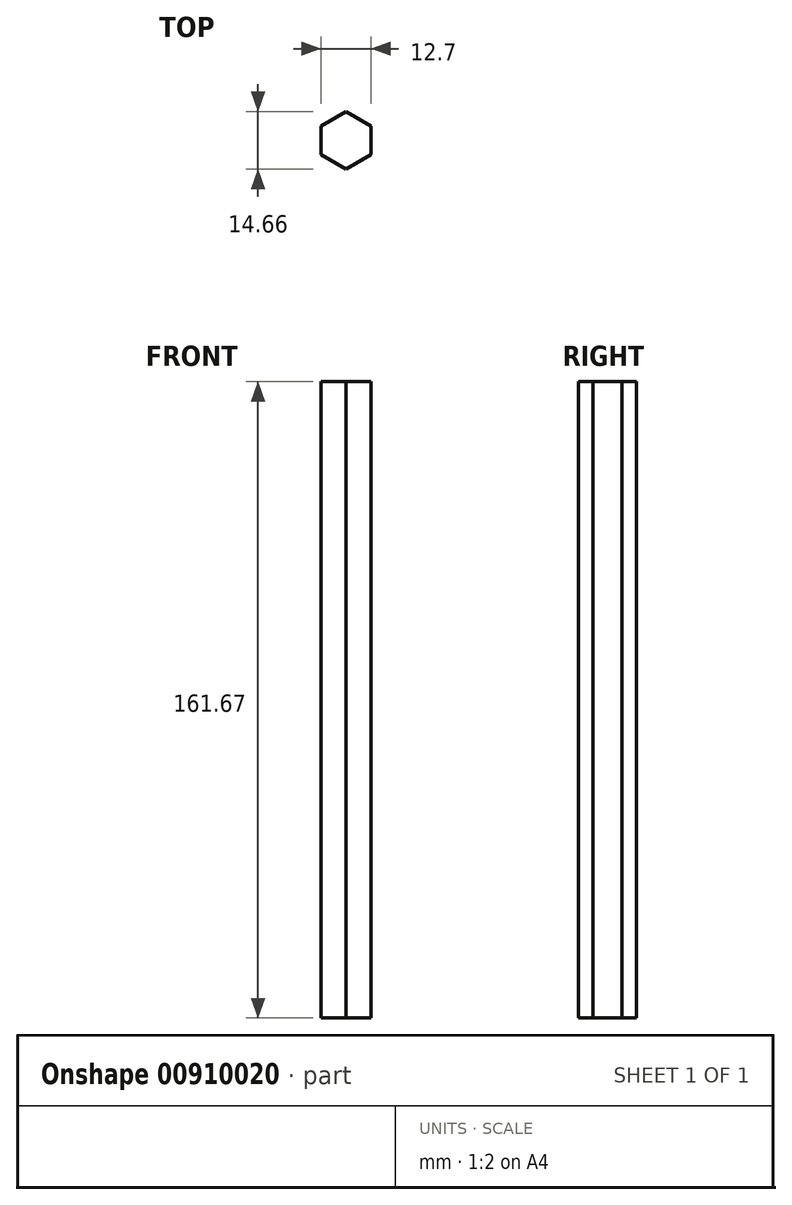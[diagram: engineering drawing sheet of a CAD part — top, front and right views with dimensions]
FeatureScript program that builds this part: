
annotation { "Feature Type Name" : "Feature", "Feature Type Description" : "" }
export const myFeature = defineFeature(function(context is Context, id is Id, definition is map)
    precondition{}
    {
        {
            var Q0;
            Q0=qCreatedBy(makeId("Top.planeOp"),FACE);
            var sketch = newSketch(context, id + "F0", { "sketchPlane" : qUnion([Q0])});
            skCircle(sketch, "E0.cCircle", {"center": v(0, 0) * mm, "radius": 6.35 * mm, "construction": true});
            skLineSegment(sketch, "E0.0", {"start": v(0, 7.33) * mm, "end": v(6.35, 3.67) * mm});
            skLineSegment(sketch, "E0.1", {"start": v(6.35, 3.67) * mm, "end": v(6.35, -3.67) * mm});
            skLineSegment(sketch, "E0.2", {"start": v(6.35, -3.67) * mm, "end": v(0, -7.33) * mm});
            skLineSegment(sketch, "E0.3", {"start": v(0, -7.33) * mm, "end": v(-6.35, -3.67) * mm});
            skLineSegment(sketch, "E0.4", {"start": v(-6.35, -3.67) * mm, "end": v(-6.35, 3.67) * mm});
            skLineSegment(sketch, "E0.5", {"start": v(-6.35, 3.67) * mm, "end": v(0, 7.33) * mm});
            skPoint(sketch, "E0.0.midPoint", {"position": v(3.18, 5.5) * mm});
            skSolve(sketch);
        }
        {
            var Q0;
            Q0=qSketchRegion(id+"F0",true);
            extrude(context, id + "F1", {"entities" : qUnion([Q0]), "depth" : 161.67 * mm, "offsetDistance" : 25.4 * mm});
        }
    });
